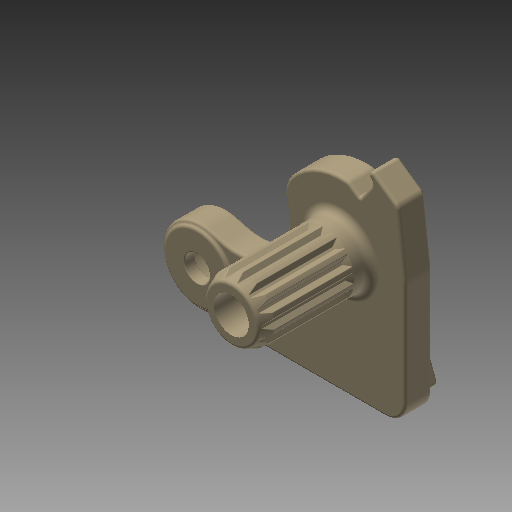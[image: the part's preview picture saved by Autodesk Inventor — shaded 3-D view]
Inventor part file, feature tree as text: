
AUTODESK INVENTOR PART (.ipt)
format: ipt  version: 2019 (Build 230136000, 136)  size: 1,617,408 bytes
history: native  units: mm
features: fillet x18, sketch x12, extrude x10, projected_geometry x4, revolve x2, chamfer x1, pattern_circular x1
ambient origin geometry x8: Origin, YZ Plane, XZ Plane, XY Plane, X Axis, Y Axis, Z Axis, Center Point
bodies: Solid1 (feature_tree)
feature tree (48):
  extrude  "Extrusion1"  Depth=21.393056mm
  fillet  "Fillet1"  Radius=33.0mm
  fillet  "Fillet2"  Radius=27.0mm
  fillet  "Fillet3"  Radius=27.0mm
  fillet  "Fillet4"  Radius=6.108652mm
  fillet  "Fillet5"  Radius=22.5mm
  extrude  "Extrusion2"  Depth=4.25mm
  fillet  "Fillet6"  Radius=20.5mm
  extrude  "Extrusion3"  Depth=16.5mm
  extrude  "Extrusion4"  Depth=6.0mm
  chamfer  "Chamfer1"  Distance=7.0mm
  fillet  "Fillet7"  Radius=7.0mm
  fillet  "Fillet8"  Radius=0.5mm
  fillet  "Fillet9"  Radius=1.0mm
  fillet  "Fillet10"  Radius=2.0mm
  fillet  "Fillet11"  Radius=5.0mm
  extrude  "Extrusion5"  Depth=0.7mm TaperAngle=0.0deg
  extrude  "Extrusion6"  Depth=0.163062mm
  extrude  "Extrusion7"  Depth=3.577898mm
  fillet  "Fillet12"  Radius=18.506898mm
  fillet  "Fillet13"  Radius=18.333232mm
  revolve  "Revolution1"  [1 undecoded]
  extrude  "Extrusion8"  Depth=6.775001mm TaperAngle=0.0deg
  extrude  "Extrusion9"  Depth=4.775001mm TaperAngle=45.0deg
  fillet  "Fillet14"  Radius=0.75mm
  fillet  "Fillet17"  Radius=0.75mm
  extrude  "Extrusion10"  Depth=0.75mm
  pattern_circular  "Circular Pattern2"  [2 undecoded]
  revolve  "Revolution2"  [1 undecoded]
  fillet  "Fillet16"  Radius=13.5mm
  fillet  "Fillet18"  Radius=4.9mm
  fillet  "Fillet19"  Radius=6.45mm
  sketch  "Sketch1"  dims[d0=36.143297mm d1=21.393056mm d2=33.0mm d3=19.0mm d4=27.0mm d5=27.0mm d6=6.108652mm d7=22.5mm]
  sketch  "Sketch2"  dims[d8=1.134464mm d9=4.25mm d10=20.5mm]
  sketch  "Sketch3"  dims[d11=2.0mm d12=16.5mm]
  sketch  "Sketch7"  dims[d13=16.5mm d14=6.0mm d15=7.0mm d16=0.0mm d17=7.0mm d18=0.5mm d19=1.0mm d20=2.0mm d21=5.0mm]
  sketch  "Sketch8"  dims[d22=17.0mm d23=0.7mm d24=0.0mm]
  sketch  "Sketch9"  dims[d25=0.75mm d26=0.163062mm]
  sketch  "Sketch10"  dims[d27=2.007156mm d28=3.577898mm d29=18.506898mm d30=18.333232mm]
  sketch  "Sketch11"  dims[d31=3.729969mm d32=24.25mm]
  sketch  "Sketch12"  dims[d33=3.0mm d34=6.775001mm d35=0.0mm]
  sketch  "Sketch13"  dims[d48=2.0mm d49=0.0mm d50=4.775001mm d51=18.575mm d52=45.0deg d53=0.75mm d54=0.75mm]
  sketch  "Sketch15"  dims[d55=0.75mm d56=0.75mm]
  projected_geometry  "Projected Loop2"
  projected_geometry  "Projected Loop3"
  sketch  "Sketch16"  dims[d57=0.75mm d58=16.04mm d59=28.0mm d60=0.0mm d61=13.5mm d62=4.9mm d63=0.0mm d64=6.45mm d65=5.474999mm d66=0.0mm d67=0.75mm d68=0.25mm d70=3.0mm d71=90.0deg d72=9.0mm d73=5.474999mm d74=0.0mm d75=16.5mm d76=1.0mm d77=0.0mm d78=0.5mm d79=1.3mm d80=0.3mm d81=0.3mm d82=1.25mm d83=1.25mm d84=23.5mm d85=0.0mm d90=130.0mm d91=54.454273mm d93=4.18879mm d94=16.04mm d95=3.0mm d96=4.5mm d97=8.5mm d98=90.0deg d99=2.0mm d100=0.8mm d101=0.2mm d102=0.2mm d103=7.0mm]
  projected_geometry  "Projected Loop4"
  projected_geometry  "Project Cut Edges1"
note: 4 required parameter values undecoded (feature->parameter linkage not recoverable at this tier; creation-order binding heuristic only, values carry confidence <= 0.55)